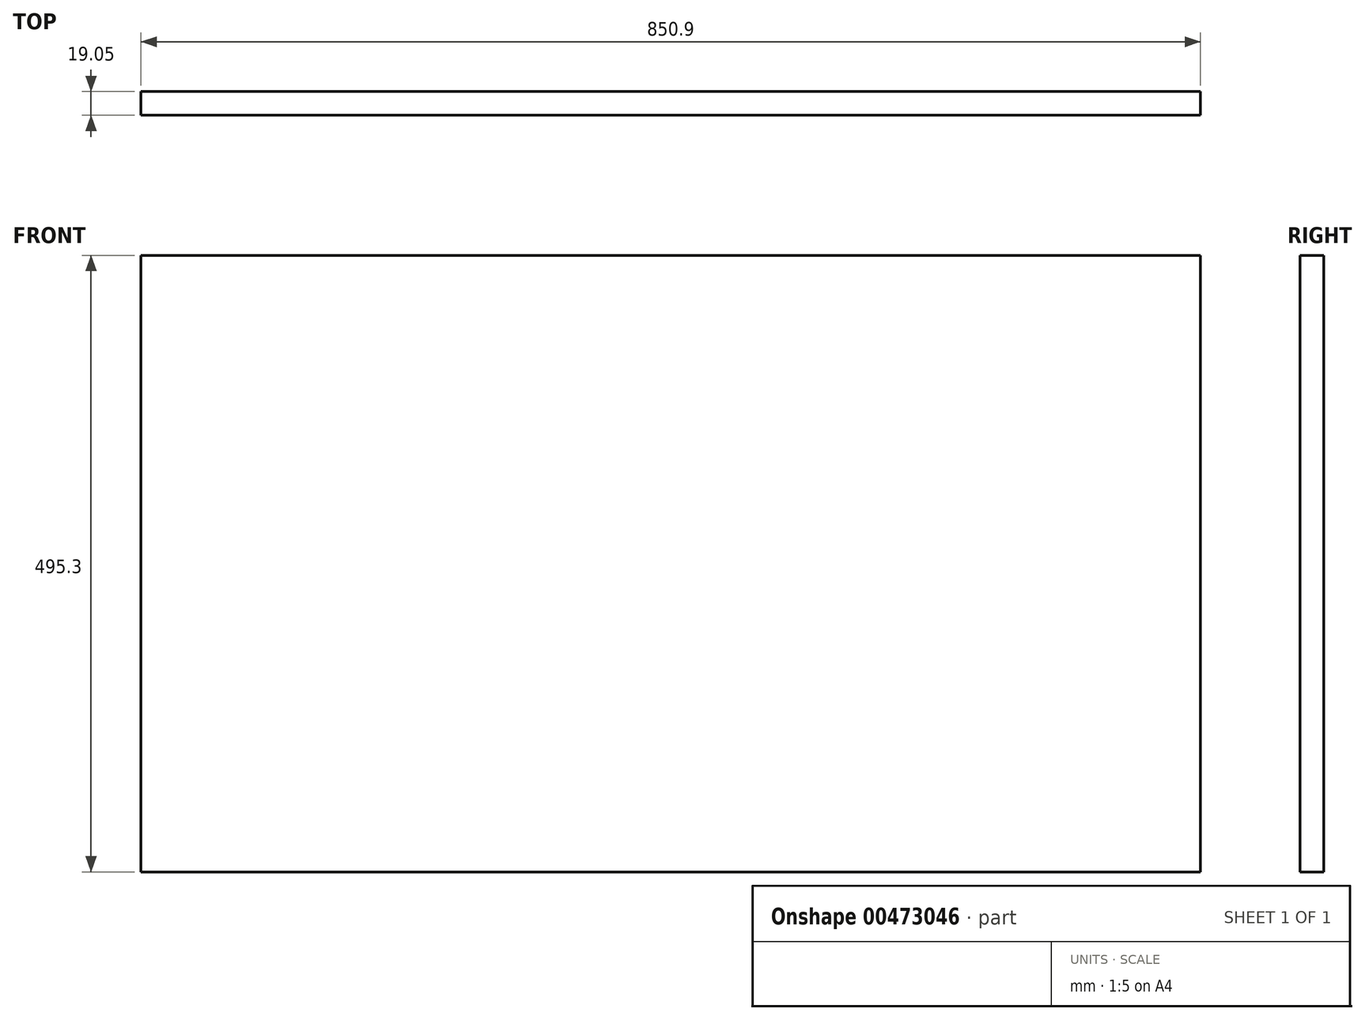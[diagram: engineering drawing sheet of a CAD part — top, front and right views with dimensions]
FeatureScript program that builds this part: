
annotation { "Feature Type Name" : "Feature", "Feature Type Description" : "" }
export const myFeature = defineFeature(function(context is Context, id is Id, definition is map)
    precondition{}
    {
        {
            var Q0;
            Q0=qCreatedBy(makeId("Front.planeOp"),FACE);
            var sketch = newSketch(context, id + "F0", { "sketchPlane" : qUnion([Q0])});
            skLineSegment(sketch, "E0.bottom", {"start": v(425.45, 247.65) * mm, "end": v(-425.45, 247.65) * mm});
            skLineSegment(sketch, "E0.top", {"start": v(425.45, -247.65) * mm, "end": v(-425.45, -247.65) * mm});
            skLineSegment(sketch, "E0.left", {"start": v(425.45, 247.65) * mm, "end": v(425.45, -247.65) * mm});
            skLineSegment(sketch, "E0.right", {"start": v(-425.45, 247.65) * mm, "end": v(-425.45, -247.65) * mm});
            skPoint(sketch, "E0.middle", {"position": v(0, 0) * mm});
            skSolve(sketch);
        }
        {
            var Q0;
            Q0=makeQuery(id+"F0.imprint","IMPRINT",FACE,{"disambiguationData":[TD([[makeQuery(id+"F0.imprint","IMPRINT",EDGE,{"derivedFrom":sQuery(id+"F0.wireOp",EDGE,"E0.bottom")}),1.0]])]});
            extrude(context, id + "F1", {"entities" : qUnion([Q0]), "depth" : 19.05 * mm});
        }
    });
